# Revit family: lgh-n15_100rxw_rxv(d)-c_60Hz
name_source: partatom
category: 機械設備
units: mm (PartAtom-declared; Revit-internal decimal feet)

## family parameters
OmniClass タイトル = Heat Exchangers for Ventilation Air
OmniClass 番号 = 23.75.10.34.21
パーツ タイプ = 標準
ロード時にボイドで切り取り = いいえ
丸型コネクタ寸法 = 直径を使用
作業面ベース = いいえ
共有 = いいえ
常に垂直 = はい
部屋計算ポイント = はい

## types (14) — shared parameters
Box_Depth = 175  [stored 0.574147 ft]
Box_Height = 261
Box_Width = 115  [stored 0.377297 ft]
Clearance Left = 600
EAダクト接続口方向_変更 = いいえ
EAダクト接続口方向_標準 = はい
IfcExportAs = IfcAirToAirHeatRecoveryType
IfcExportType = ROTARYWHEEL
OAダクト接続口方向_変更 = いいえ
OAダクト接続口方向_標準 = はい
OmniClassCode = 23-27 23 19 11
Sensor_Depth = 115  [stored 0.377297 ft]
Sensor_Height = 183
Sensor_Width = 184  [stored 0.603675 ft]
URL = https://www.mitsubishielectric.co.jp
Uniclass2015Code = Pr_60_60_36_88
Uniclass2015Title = Thermal wheels
Uniclass2015Version = Systems v1.9
メンテナンススペース = はい
仕様書バージョン = Version1.0
企業コード = 108420
分類コード = 50052504100070
初期抵抗 = 0.0 Pa
周波数 = 60 Hz
呼称 = 全熱交換ユニット
外気量 = 0.0 m³/h
天吊金具_幅 = 20  [stored 0.0656168 ft]
天吊金具_径 = 7  [stored 0.0229659 ft]
実風量 = 0.0 m³/h
形式 = 天井埋込ダクト形
排気量 = 0.0 m³/h
本体マテリアル = 溶融亜鉛めっき鋼板
法定耐用年数 = 15
点検口 = はい
点検口_Depth = 450
点検口離隔 = 150
相 = 1
積算_科目 = 1 空気調和設備
符号 = HEU
製品リリース年月 = 2020/10/1
製品出荷対象 = 国内
製造元 = 三菱電機株式会社
設置方法 = 天井吊(隠ぺい)形
設計風量 = 0.0 m³/h
説明 = 業務用ロスナイ 天井埋込形 DCマイコン CO2センサー付
負荷分類 = 3_ファン類
運転質量 = 0.00 kg
電動機出力 = 0 W
zero-valued in all types: Clearance Bottom, Clearance Top, EAサイズ_W, OAサイズ_W

## per-type parameters (varying)
- LGH-N15RXW-C_100V: Box_D=33  [stored 0.108268 ft]; Box_H=15  [stored 0.0492126 ft]; Depth=780; DuctChange_Center=118; Duct_Depth=59; Duct_Height=145  [stored 0.475722 ft]; Duct_Pitch=435; EAサイズ_D=98; Height=290; MAX静圧=180.0 Pa; MAX風量=150.0 m³/h; MID静圧=93.0 Pa; MID風量=108.0 m³/h; MIN静圧=35.0 Pa; MIN風量=66.0 m³/h; OAサイズ_D=98; RAサイズ_D=98; SAサイズ_D=98; SMAX静圧=210.0 Pa; SMAX風量=150.0 m³/h; Sensor_D=69  [stored 0.226378 ft]; Sensor_H=14  [stored 0.0459318 ft]; Width=610; エンタルピ交換効率_冷房=64.50%; エンタルピ交換効率_暖房=75.50%; モデル=LGH-N15RXW-C; 価格=402200 $; 参照している仕様書等のバージョン=公共建築工事標準仕様書（機械設備工事編）平成31年度版; 天吊金具_高さ=65  [stored 0.213255 ft]; 天吊金具ピッチ1=670; 天吊金具ピッチ2=780; 極数=2; 機外静圧=210.0 Pa; 機外静圧_排気=210.0 Pa; 消費電力=85 W; 温度交換効率=74.00%; 点検口高さ=-290  [stored -0.951444 ft]; 製品質量=23.00 kg; 質量=27.60 kg; 電圧=100 V; 面風速=5.3 m/s; 風量=150.0 m³/h; 騒音レベル(dB(A))=31
- LGH-N15RXW-C_200V: Box_D=33  [stored 0.108268 ft]; Box_H=15  [stored 0.0492126 ft]; Depth=780; DuctChange_Center=118; Duct_Depth=59; Duct_Height=145  [stored 0.475722 ft]; Duct_Pitch=435; EAサイズ_D=98; Height=290; MAX静圧=180.0 Pa; MAX風量=150.0 m³/h; MID静圧=93.0 Pa; MID風量=108.0 m³/h; MIN静圧=35.0 Pa; MIN風量=66.0 m³/h; OAサイズ_D=98; RAサイズ_D=98; SAサイズ_D=98; SMAX静圧=210.0 Pa; SMAX風量=150.0 m³/h; Sensor_D=69  [stored 0.226378 ft]; Sensor_H=14  [stored 0.0459318 ft]; Width=610; エンタルピ交換効率_冷房=64.50%; エンタルピ交換効率_暖房=75.50%; モデル=LGH-N15RXW-C; 価格=402200 $; 参照している仕様書等のバージョン=公共建築工事標準仕様書（機械設備工事編）平成31年度版; 天吊金具_高さ=65  [stored 0.213255 ft]; 天吊金具ピッチ1=670; 天吊金具ピッチ2=780; 極数=3; 機外静圧=210.0 Pa; 機外静圧_排気=210.0 Pa; 消費電力=85 W; 温度交換効率=74.00%; 点検口高さ=-290  [stored -0.951444 ft]; 製品質量=23.00 kg; 質量=27.60 kg; 電圧=200 V; 面風速=5.3 m/s; 風量=150.0 m³/h; 騒音レベル(dB(A))=31
- LGH-N25RXW-C_100V: Box_D=33  [stored 0.108268 ft]; Box_H=15  [stored 0.0492126 ft]; Depth=780; DuctChange_Center=118; Duct_Depth=69  [stored 0.226378 ft]; Duct_Height=145  [stored 0.475722 ft]; Duct_Pitch=520; EAサイズ_D=142  [stored 0.465879 ft]; Height=290; MAX静圧=145.0 Pa; MAX風量=250.0 m³/h; MID静圧=75.0 Pa; MID風量=180.0 m³/h; MIN静圧=28.0 Pa; MIN風量=110.0 m³/h; OAサイズ_D=142  [stored 0.465879 ft]; RAサイズ_D=142  [stored 0.465879 ft]; SAサイズ_D=142  [stored 0.465879 ft]; SMAX静圧=170.0 Pa; SMAX風量=250.0 m³/h; Sensor_D=69  [stored 0.226378 ft]; Sensor_H=14  [stored 0.0459318 ft]; Width=735; エンタルピ交換効率_冷房=63.00%; エンタルピ交換効率_暖房=73.00%; モデル=LGH-N25RXW-C; 価格=422200 $; 参照している仕様書等のバージョン=公共建築工事標準仕様書（機械設備工事編）平成31年度版; 天吊金具_高さ=65  [stored 0.213255 ft]; 天吊金具ピッチ1=795; 天吊金具ピッチ2=780; 極数=2; 機外静圧=170.0 Pa; 機外静圧_排気=170.0 Pa; 消費電力=110 W; 温度交換効率=70.00%; 点検口高さ=-290  [stored -0.951444 ft]; 製品質量=24.00 kg; 質量=28.80 kg; 電圧=100 V; 面風速=3.9 m/s; 風量=250.0 m³/h; 騒音レベル(dB(A))=30
- LGH-N25RXW-C_200V: Box_D=33  [stored 0.108268 ft]; Box_H=15  [stored 0.0492126 ft]; Depth=780; DuctChange_Center=118; Duct_Depth=69  [stored 0.226378 ft]; Duct_Height=145  [stored 0.475722 ft]; Duct_Pitch=520; EAサイズ_D=142  [stored 0.465879 ft]; Height=290; MAX静圧=145.0 Pa; MAX風量=250.0 m³/h; MID静圧=75.0 Pa; MID風量=180.0 m³/h; MIN静圧=28.0 Pa; MIN風量=110.0 m³/h; OAサイズ_D=142  [stored 0.465879 ft]; RAサイズ_D=142  [stored 0.465879 ft]; SAサイズ_D=142  [stored 0.465879 ft]; SMAX静圧=170.0 Pa; SMAX風量=250.0 m³/h; Sensor_D=69  [stored 0.226378 ft]; Sensor_H=14  [stored 0.0459318 ft]; Width=735; エンタルピ交換効率_冷房=63.00%; エンタルピ交換効率_暖房=73.00%; モデル=LGH-N25RXW-C; 価格=422200 $; 参照している仕様書等のバージョン=公共建築工事標準仕様書（機械設備工事編）平成31年度版; 天吊金具_高さ=65  [stored 0.213255 ft]; 天吊金具ピッチ1=795; 天吊金具ピッチ2=780; 極数=3; 機外静圧=170.0 Pa; 機外静圧_排気=170.0 Pa; 消費電力=110 W; 温度交換効率=70.00%; 点検口高さ=-290  [stored -0.951444 ft]; 製品質量=24.00 kg; 質量=28.80 kg; 電圧=200 V; 面風速=3.9 m/s; 風量=250.0 m³/h; 騒音レベル(dB(A))=30
- LGH-N35RXW-C_100V: Box_D=68; Box_H=23  [stored 0.0754593 ft]; Depth=890; DuctChange_Center=140  [stored 0.459318 ft]; Duct_Depth=69  [stored 0.226378 ft]; Duct_Height=165; Duct_Pitch=600; EAサイズ_D=142  [stored 0.465879 ft]; Height=330; MAX静圧=185.0 Pa; MAX風量=350.0 m³/h; MID静圧=96.0 Pa; MID風量=252.0 m³/h; MIN静圧=36.0 Pa; MIN風量=154.0 m³/h; OAサイズ_D=142  [stored 0.465879 ft]; RAサイズ_D=142  [stored 0.465879 ft]; SAサイズ_D=142  [stored 0.465879 ft]; SMAX静圧=300.0 Pa; SMAX風量=350.0 m³/h; Sensor_D=104; Sensor_H=22  [stored 0.0721785 ft]; Width=875; エンタルピ交換効率_冷房=65.50%; エンタルピ交換効率_暖房=74.50%; モデル=LGH-N35RXW-C; 価格=445200 $; 参照している仕様書等のバージョン=公共建築工事標準仕様書（機械設備工事編）平成31年度版; 天吊金具_高さ=70  [stored 0.229659 ft]; 天吊金具ピッチ1=935; 天吊金具ピッチ2=890; 極数=2; 機外静圧=300.0 Pa; 機外静圧_排気=300.0 Pa; 消費電力=210 W; 温度交換効率=71.50%; 点検口高さ=-330; 製品質量=33.00 kg; 質量=39.60 kg; 電圧=100 V; 面風速=5.5 m/s; 風量=350.0 m³/h; 騒音レベル(dB(A))=33
- LGH-N35RXW-C_200V: Box_D=68; Box_H=23  [stored 0.0754593 ft]; Depth=890; DuctChange_Center=140  [stored 0.459318 ft]; Duct_Depth=69  [stored 0.226378 ft]; Duct_Height=165; Duct_Pitch=600; EAサイズ_D=142  [stored 0.465879 ft]; Height=330; MAX静圧=185.0 Pa; MAX風量=350.0 m³/h; MID静圧=96.0 Pa; MID風量=252.0 m³/h; MIN静圧=36.0 Pa; MIN風量=154.0 m³/h; OAサイズ_D=142  [stored 0.465879 ft]; RAサイズ_D=142  [stored 0.465879 ft]; SAサイズ_D=142  [stored 0.465879 ft]; SMAX静圧=300.0 Pa; SMAX風量=350.0 m³/h; Sensor_D=104; Sensor_H=22  [stored 0.0721785 ft]; Width=875; エンタルピ交換効率_冷房=65.50%; エンタルピ交換効率_暖房=74.50%; モデル=LGH-N35RXW-C; 価格=445200 $; 参照している仕様書等のバージョン=公共建築工事標準仕様書（機械設備工事編）平成31年度版; 天吊金具_高さ=70  [stored 0.229659 ft]; 天吊金具ピッチ1=935; 天吊金具ピッチ2=890; 極数=3; 機外静圧=300.0 Pa; 機外静圧_排気=300.0 Pa; 消費電力=210 W; 温度交換効率=71.50%; 点検口高さ=-330; 製品質量=33.00 kg; 質量=39.60 kg; 電圧=200 V; 面風速=5.5 m/s; 風量=350.0 m³/h; 騒音レベル(dB(A))=33
- LGH-N50RXW-C_100V: Box_D=68; Box_H=23  [stored 0.0754593 ft]; Depth=890; DuctChange_Center=130  [stored 0.426509 ft]; Duct_Depth=84  [stored 0.275591 ft]; Duct_Height=165; Duct_Pitch=700; EAサイズ_D=192; Height=330; MAX静圧=190.0 Pa; MAX風量=500.0 m³/h; MID静圧=98.0 Pa; MID風量=360.0 m³/h; MIN静圧=37.0 Pa; MIN風量=220.0 m³/h; OAサイズ_D=192; RAサイズ_D=192; SAサイズ_D=192; SMAX静圧=310.0 Pa; SMAX風量=500.0 m³/h; Sensor_D=104; Sensor_H=22  [stored 0.0721785 ft]; Width=1020; エンタルピ交換効率_冷房=63.00%; エンタルピ交換効率_暖房=73.00%; モデル=LGH-N50RXW-C; 価格=503200 $; 参照している仕様書等のバージョン=公共建築工事標準仕様書（機械設備工事編）平成31年度版; 天吊金具_高さ=70  [stored 0.229659 ft]; 天吊金具ピッチ1=1080; 天吊金具ピッチ2=890; 極数=2; 機外静圧=310.0 Pa; 機外静圧_排気=310.0 Pa; 消費電力=315 W; 温度交換効率=71.00%; 点検口高さ=-330; 製品質量=37.00 kg; 質量=44.40 kg; 電圧=100 V; 面風速=4.4 m/s; 風量=500.0 m³/h; 騒音レベル(dB(A))=37
- LGH-N50RXW-C_200V: Box_D=68; Box_H=23  [stored 0.0754593 ft]; Depth=890; DuctChange_Center=130  [stored 0.426509 ft]; Duct_Depth=84  [stored 0.275591 ft]; Duct_Height=165; Duct_Pitch=700; EAサイズ_D=192; Height=330; MAX静圧=190.0 Pa; MAX風量=500.0 m³/h; MID静圧=98.0 Pa; MID風量=360.0 m³/h; MIN静圧=37.0 Pa; MIN風量=220.0 m³/h; OAサイズ_D=192; RAサイズ_D=192; SAサイズ_D=192; SMAX静圧=310.0 Pa; SMAX風量=500.0 m³/h; Sensor_D=104; Sensor_H=22  [stored 0.0721785 ft]; Width=1020; エンタルピ交換効率_冷房=63.00%; エンタルピ交換効率_暖房=73.00%; モデル=LGH-N50RXW-C; 価格=503200 $; 参照している仕様書等のバージョン=公共建築工事標準仕様書（機械設備工事編）平成31年度版; 天吊金具_高さ=70  [stored 0.229659 ft]; 天吊金具ピッチ1=1080; 天吊金具ピッチ2=890; 極数=3; 機外静圧=310.0 Pa; 機外静圧_排気=310.0 Pa; 消費電力=315 W; 温度交換効率=71.00%; 点検口高さ=-330; 製品質量=37.00 kg; 質量=44.40 kg; 電圧=200 V; 面風速=4.4 m/s; 風量=500.0 m³/h; 騒音レベル(dB(A))=37
- LGH-N65RXW-C_100V: Box_D=71  [stored 0.23294 ft]; Box_H=57  [stored 0.187008 ft]; Depth=984; DuctChange_Center=122  [stored 0.400262 ft]; Duct_Depth=84  [stored 0.275591 ft]; Duct_Height=202; Duct_Pitch=620; EAサイズ_D=192; Height=404; MAX静圧=230.0 Pa; MAX風量=650.0 m³/h; MID静圧=119.0 Pa; MID風量=468.0 m³/h; MIN静圧=45.0 Pa; MIN風量=286.0 m³/h; OAサイズ_D=192; RAサイズ_D=192; SAサイズ_D=192; SMAX静圧=320.0 Pa; SMAX風量=650.0 m³/h; Sensor_D=107  [stored 0.35105 ft]; Sensor_H=56  [stored 0.183727 ft]; Width=892; エンタルピ交換効率_冷房=63.00%; エンタルピ交換効率_暖房=72.00%; モデル=LGH-N65RXW-C; 価格=608200 $; 参照している仕様書等のバージョン=公共建築工事標準仕様書（機械設備工事編）平成31年度版; 天吊金具_高さ=76  [stored 0.249344 ft]; 天吊金具ピッチ1=952; 天吊金具ピッチ2=984; 極数=2; 機外静圧=320.0 Pa; 機外静圧_排気=320.0 Pa; 消費電力=445 W; 温度交換効率=71.50%; 点検口高さ=-404  [stored -1.32546 ft]; 製品質量=43.00 kg; 質量=51.60 kg; 電圧=100 V; 面風速=5.8 m/s; 風量=650.0 m³/h; 騒音レベル(dB(A))=40
- LGH-N65RXW-C_200V: Box_D=71  [stored 0.23294 ft]; Box_H=57  [stored 0.187008 ft]; Depth=984; DuctChange_Center=122  [stored 0.400262 ft]; Duct_Depth=84  [stored 0.275591 ft]; Duct_Height=202; Duct_Pitch=620; EAサイズ_D=192; Height=404; MAX静圧=230.0 Pa; MAX風量=650.0 m³/h; MID静圧=119.0 Pa; MID風量=468.0 m³/h; MIN静圧=45.0 Pa; MIN風量=286.0 m³/h; OAサイズ_D=192; RAサイズ_D=192; SAサイズ_D=192; SMAX静圧=320.0 Pa; SMAX風量=650.0 m³/h; Sensor_D=107  [stored 0.35105 ft]; Sensor_H=56  [stored 0.183727 ft]; Width=892; エンタルピ交換効率_冷房=63.00%; エンタルピ交換効率_暖房=72.00%; モデル=LGH-N65RXW-C; 価格=608200 $; 参照している仕様書等のバージョン=公共建築工事標準仕様書（機械設備工事編）平成31年度版; 天吊金具_高さ=76  [stored 0.249344 ft]; 天吊金具ピッチ1=952; 天吊金具ピッチ2=984; 極数=3; 機外静圧=320.0 Pa; 機外静圧_排気=320.0 Pa; 消費電力=445 W; 温度交換効率=71.50%; 点検口高さ=-404  [stored -1.32546 ft]; 製品質量=43.00 kg; 質量=51.60 kg; 電圧=200 V; 面風速=5.8 m/s; 風量=650.0 m³/h; 騒音レベル(dB(A))=40
- LGH-N80RXV-C: Box_D=146  [stored 0.479003 ft]; Box_H=88  [stored 0.288714 ft]; Depth=1144; DuctChange_Center=165; Duct_Depth=84  [stored 0.275591 ft]; Duct_Height=202; Duct_Pitch=690; EAサイズ_D=242; Height=404; MAX静圧=190.0 Pa; MAX風量=800.0 m³/h; MID静圧=98.0 Pa; MID風量=576.0 m³/h; MIN静圧=37.0 Pa; MIN風量=352.0 m³/h; OAサイズ_D=242; RAサイズ_D=242; SAサイズ_D=242; SMAX静圧=310.0 Pa; SMAX風量=800.0 m³/h; Sensor_D=182  [stored 0.597113 ft]; Sensor_H=87  [stored 0.285433 ft]; Width=1004; エンタルピ交換効率_冷房=65.00%; エンタルピ交換効率_暖房=75.00%; モデル=LGH-N80RXV-C; 価格=688200 $; 参照している仕様書等のバージョン=公共建築工事標準仕様書（機械設備工事編）平成31年度版; 天吊金具_高さ=76  [stored 0.249344 ft]; 天吊金具ピッチ1=1064; 天吊金具ピッチ2=1144; 極数=2; 機外静圧=310.0 Pa; 機外静圧_排気=310.0 Pa; 消費電力=540 W; 温度交換効率=73.00%; 点検口高さ=-404  [stored -1.32546 ft]; 製品質量=53.00 kg; 質量=63.60 kg; 電圧=100 V; 面風速=4.5 m/s; 風量=800.0 m³/h; 騒音レベル(dB(A))=40
- LGH-N80RXVD-C: Box_D=146  [stored 0.479003 ft]; Box_H=88  [stored 0.288714 ft]; Depth=1144; DuctChange_Center=165; Duct_Depth=84  [stored 0.275591 ft]; Duct_Height=202; Duct_Pitch=690; EAサイズ_D=242; Height=404; MAX静圧=190.0 Pa; MAX風量=800.0 m³/h; MID静圧=98.0 Pa; MID風量=576.0 m³/h; MIN静圧=37.0 Pa; MIN風量=352.0 m³/h; OAサイズ_D=242; RAサイズ_D=242; SAサイズ_D=242; SMAX静圧=310.0 Pa; SMAX風量=800.0 m³/h; Sensor_D=182  [stored 0.597113 ft]; Sensor_H=87  [stored 0.285433 ft]; Width=1004; エンタルピ交換効率_冷房=65.00%; エンタルピ交換効率_暖房=75.00%; モデル=LGH-N80RXVD-C; 価格=688200 $; 参照している仕様書等のバージョン=公共建築工事標準仕様書（機械設備工事編）平成31年度版; 天吊金具_高さ=76  [stored 0.249344 ft]; 天吊金具ピッチ1=1064; 天吊金具ピッチ2=1144; 極数=3; 機外静圧=310.0 Pa; 機外静圧_排気=310.0 Pa; 消費電力=540 W; 温度交換効率=73.00%; 点検口高さ=-404  [stored -1.32546 ft]; 製品質量=53.00 kg; 質量=63.60 kg; 電圧=200 V; 面風速=4.5 m/s; 風量=800.0 m³/h; 騒音レベル(dB(A))=40
- LGH-N100RXV-C: Box_D=146  [stored 0.479003 ft]; Box_H=88  [stored 0.288714 ft]; Depth=1144; DuctChange_Center=165; Duct_Depth=84  [stored 0.275591 ft]; Duct_Height=202; Duct_Pitch=917; EAサイズ_D=242; Height=404; MAX静圧=165.0 Pa; MAX風量=1000.0 m³/h; MID静圧=86.0 Pa; MID風量=720.0 m³/h; MIN静圧=32.0 Pa; MIN風量=440.0 m³/h; OAサイズ_D=242; RAサイズ_D=242; SAサイズ_D=242; SMAX静圧=225.0 Pa; SMAX風量=1000.0 m³/h; Sensor_D=182  [stored 0.597113 ft]; Sensor_H=87  [stored 0.285433 ft]; Width=1231; エンタルピ交換効率_冷房=65.00%; エンタルピ交換効率_暖房=75.00%; モデル=LGH-N100RXV-C; 価格=757200 $; 天吊金具_高さ=76  [stored 0.249344 ft]; 天吊金具ピッチ1=1291; 天吊金具ピッチ2=1144; 極数=2; 機外静圧=225.0 Pa; 機外静圧_排気=225.0 Pa; 消費電力=580 W; 温度交換効率=73.00%; 点検口高さ=-404  [stored -1.32546 ft]; 製品質量=58.00 kg; 質量=69.60 kg; 電圧=100 V; 面風速=5.7 m/s; 風量=1000.0 m³/h; 騒音レベル(dB(A))=38
- LGH-N100RXVD-C: Box_D=146  [stored 0.479003 ft]; Box_H=88  [stored 0.288714 ft]; Depth=1144; DuctChange_Center=165; Duct_Depth=84  [stored 0.275591 ft]; Duct_Height=202; Duct_Pitch=917; EAサイズ_D=242; Height=404; MAX静圧=165.0 Pa; MAX風量=1000.0 m³/h; MID静圧=86.0 Pa; MID風量=720.0 m³/h; MIN静圧=32.0 Pa; MIN風量=440.0 m³/h; OAサイズ_D=242; RAサイズ_D=242; SAサイズ_D=242; SMAX静圧=225.0 Pa; SMAX風量=1000.0 m³/h; Sensor_D=182  [stored 0.597113 ft]; Sensor_H=87  [stored 0.285433 ft]; Width=1231; エンタルピ交換効率_冷房=65.00%; エンタルピ交換効率_暖房=75.00%; モデル=LGH-N100RXVD-C; 価格=757200 $; 天吊金具_高さ=76  [stored 0.249344 ft]; 天吊金具ピッチ1=1291; 天吊金具ピッチ2=1144; 極数=3; 機外静圧=225.0 Pa; 機外静圧_排気=225.0 Pa; 消費電力=580 W; 温度交換効率=73.00%; 点検口高さ=-404  [stored -1.32546 ft]; 製品質量=58.00 kg; 質量=69.60 kg; 電圧=200 V; 面風速=5.7 m/s; 風量=1000.0 m³/h; 騒音レベル(dB(A))=38

note: [stored X ft] marks values corroborated as IEEE doubles in the binary element streams (Revit-internal decimal feet)

## geometry (parser evidence)
native form markers: Blend x4
no freeform markers — native parametric forms only
